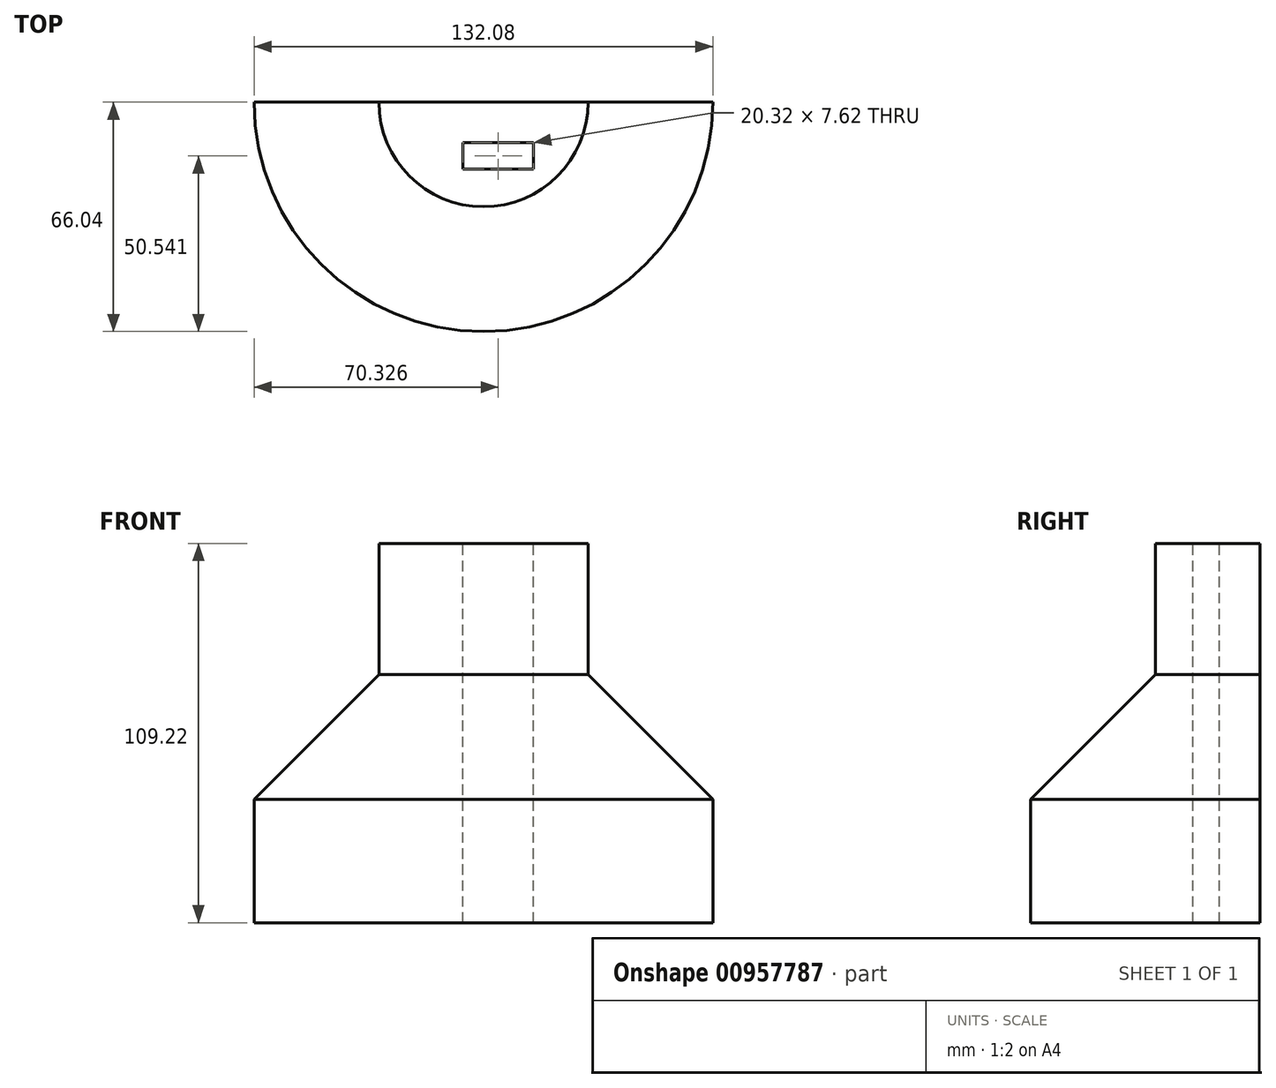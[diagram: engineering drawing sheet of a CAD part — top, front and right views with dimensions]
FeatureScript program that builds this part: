
annotation { "Feature Type Name" : "Feature", "Feature Type Description" : "" }
export const myFeature = defineFeature(function(context is Context, id is Id, definition is map)
    precondition{}
    {
        {
            var Q0;
            Q0=qCreatedBy(makeId("Front.planeOp"),FACE);
            var sketch = newSketch(context, id + "F0", { "sketchPlane" : qUnion([Q0])});
            skLineSegment(sketch, "E0", {"start": v(-30.12, 57.58) * mm, "end": v(-30.12, 19.85) * mm});
            skLineSegment(sketch, "E1", {"start": v(-30.12, 19.85) * mm, "end": v(-66.04, -16.08) * mm});
            skLineSegment(sketch, "E2", {"start": v(-66.04, -16.08) * mm, "end": v(-66.04, -51.64) * mm});
            skLineSegment(sketch, "E3", {"start": v(-66.04, -51.64) * mm, "end": v(0, -51.64) * mm});
            skLineSegment(sketch, "E4", {"start": v(0, -51.64) * mm, "end": v(0, 57.58) * mm});
            skLineSegment(sketch, "E5", {"start": v(0, 57.58) * mm, "end": v(-30.12, 57.58) * mm});
            skSolve(sketch);
        }
        {
            var Q0;
            Q0=makeQuery(id+"F0.imprint","IMPRINT",FACE,{"disambiguationData":[TD([[makeQuery(id+"F0.imprint","IMPRINT",EDGE,{"derivedFrom":sQuery(id+"F0.wireOp",EDGE,"E0")}),1.0]])]});
            var Q1;
            Q1=sQuery(id+"F0.wireOp",EDGE,"E4");
            revolve(context, id + "F1", {"surfaceOperationType" : NewSurfaceOperationType.NEW, "entities" : qUnion([Q0]), "axis" : qUnion([Q1]), "revolveType" : RevolveType.ONE_DIRECTION, "angle" : 180 * degree});
        }
        {
            var Q0;
            Q0=makeQuery(id+"F1.opRevolve","SWEPT_FACE",FACE,{"disambiguationData":[OSD([sQuery(id+"F0.wireOp",EDGE,"E5")])]});
            var sketch = newSketch(context, id + "F2", { "sketchPlane" : qUnion([Q0])});
            skLineSegment(sketch, "E6.bottom", {"start": v(-5.87, -11.69) * mm, "end": v(14.45, -11.69) * mm});
            skLineSegment(sketch, "E6.top", {"start": v(-5.87, -19.3) * mm, "end": v(14.45, -19.3) * mm});
            skLineSegment(sketch, "E6.left", {"start": v(-5.87, -11.69) * mm, "end": v(-5.87, -19.3) * mm});
            skLineSegment(sketch, "E6.right", {"start": v(14.45, -11.69) * mm, "end": v(14.45, -19.3) * mm});
            skSolve(sketch);
        }
        {
            var Q0;
            Q0=makeQuery(id+"F2.imprint","IMPRINT",FACE,{"disambiguationData":[TD([[makeQuery(id+"F2.imprint","IMPRINT",EDGE,{"derivedFrom":sQuery(id+"F2.wireOp",EDGE,"E6.bottom")}),-1.0]])]});
            extrude(context, id + "F3", {"entities" : qUnion([Q0]), "operationType" : NewBodyOperationType.REMOVE, "endBound" : BoundingType.THROUGH_ALL, "oppositeDirection" : true, "depth" : 25.4 * mm, "offsetDistance" : 25.4 * mm});
        }
    });
